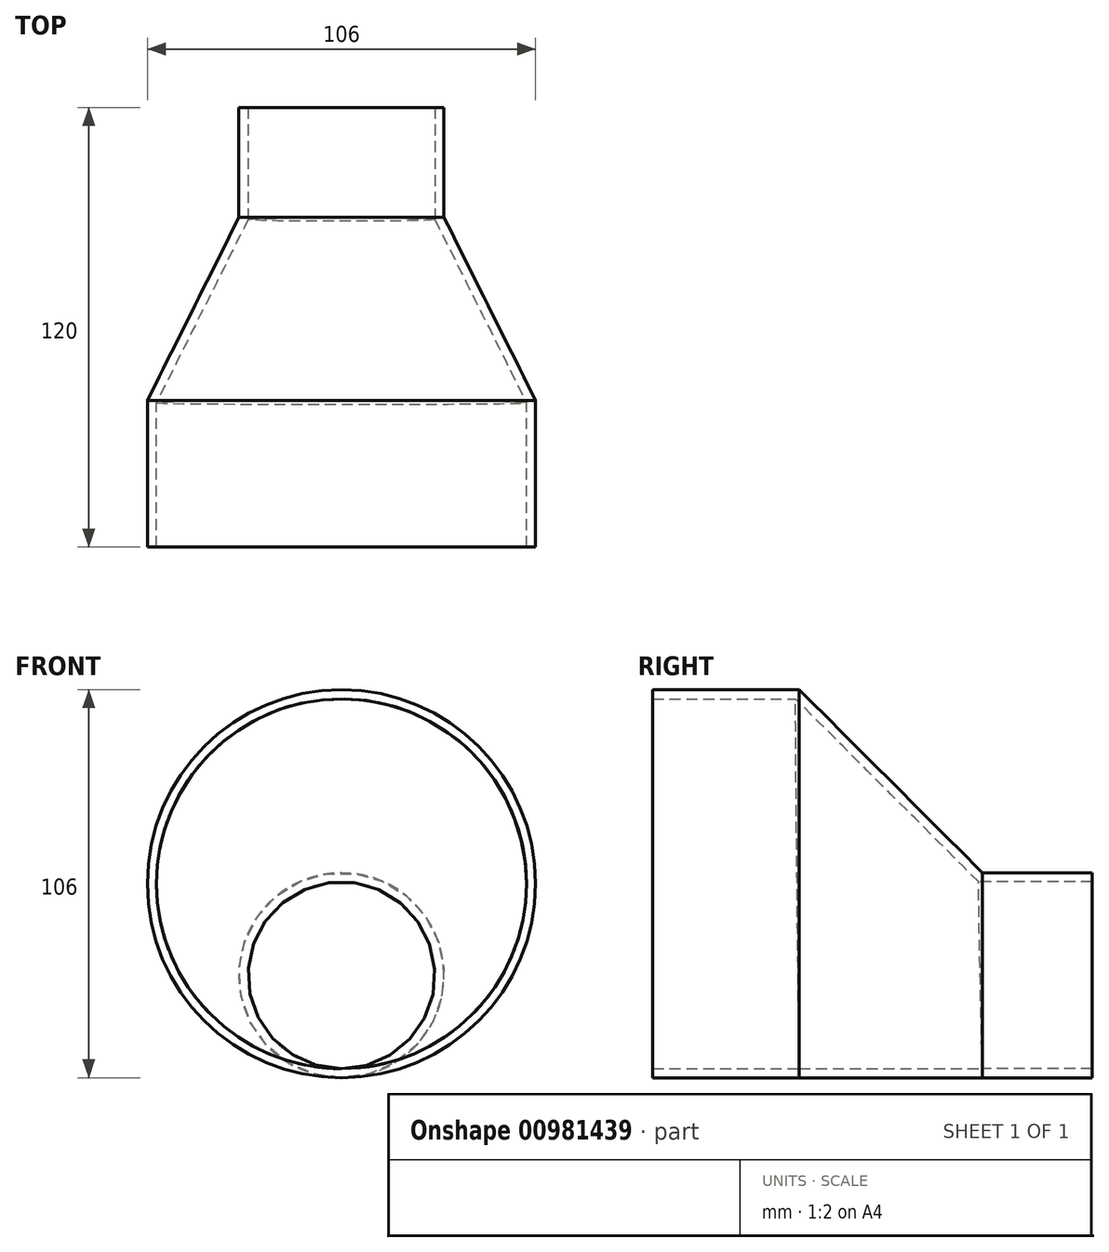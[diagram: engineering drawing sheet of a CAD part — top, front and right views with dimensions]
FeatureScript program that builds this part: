
annotation { "Feature Type Name" : "Feature", "Feature Type Description" : "" }
export const myFeature = defineFeature(function(context is Context, id is Id, definition is map)
    precondition{}
    {
        {
            var Q0;
            Q0=qCreatedBy(makeId("Front.planeOp"),FACE);
            var sketch = newSketch(context, id + "F0", { "sketchPlane" : qUnion([Q0])});
            skCircle(sketch, "E0", {"center": v(0, 0) * mm, "radius": 50 * mm});
            skCircle(sketch, "E1", {"center": v(0, 0) * mm, "radius": 53 * mm});
            skSolve(sketch);
        }
        {
            var Q0;
            Q0=makeQuery(id+"F0.imprint","IMPRINT",FACE,{"disambiguationData":[TD([[makeQuery(id+"F0.imprint","IMPRINT",EDGE,{"derivedFrom":sQuery(id+"F0.wireOp",EDGE,"E0")}),-1.0]])]});
            var Q1;
            Q1=makeQuery(id+"F0.imprint","IMPRINT",FACE,{"disambiguationData":[TD([[makeQuery(id+"F0.imprint","IMPRINT",EDGE,{"derivedFrom":sQuery(id+"F0.wireOp",EDGE,"E0")}),1.0]])]});
            extrude(context, id + "F1", {"entities" : qUnion([Q0, Q1]), "depth" : 40 * mm, "offsetDistance" : 25 * mm});
        }
        {
            var Q0;
            Q0=qCreatedBy(makeId("Front.planeOp"),FACE);
            cPlane(context, id + "F2", {"entities" : qUnion([Q0]), "cplaneType" : CPlaneType.OFFSET, "offset" : 50 * mm, "oppositeDirection" : true, "width" : 150 * mm, "height" : 150 * mm});
        }
        {
            var Q0;
            Q0=qCreatedBy(id+"F2.planeOp",FACE);
            var sketch = newSketch(context, id + "F3", { "sketchPlane" : qUnion([Q0])});
            skCircle(sketch, "E2", {"center": v(0, -25) * mm, "radius": 25 * mm});
            skCircle(sketch, "E3", {"center": v(0, -25) * mm, "radius": 28 * mm});
            skSolve(sketch);
        }
        {
            var Q0;
            Q0=makeQuery(id+"F3.imprint","IMPRINT",FACE,{"disambiguationData":[TD([[makeQuery(id+"F3.imprint","IMPRINT",EDGE,{"derivedFrom":sQuery(id+"F3.wireOp",EDGE,"E2")}),-1.0]])]});
            var Q1;
            Q1=makeQuery(id+"F3.imprint","IMPRINT",FACE,{"disambiguationData":[TD([[makeQuery(id+"F3.imprint","IMPRINT",EDGE,{"derivedFrom":sQuery(id+"F3.wireOp",EDGE,"E2")}),1.0]])]});
            extrude(context, id + "F4", {"entities" : qUnion([Q0, Q1]), "oppositeDirection" : true, "depth" : 30 * mm, "offsetDistance" : 25 * mm});
        }
        {
            var Q0;
            Q0=makeQuery(id+"F1.opExtrude","CAP_FACE",FACE,{"disambiguationData":[OSD([sQuery(id+"F0.wireOp",EDGE,"E1")])],"isStart":true});
            var Q1;
            Q1=makeQuery(id+"F4.opExtrude","CAP_FACE",FACE,{"disambiguationData":[OSD([sQuery(id+"F3.wireOp",EDGE,"E3")])],"isStart":true});
            loft(context, id + "F5", {"operationType" : NewBodyOperationType.ADD, "sheetProfilesArray" : [{ "sheetProfileEntities" : qUnion([Q0]) }, { "sheetProfileEntities" : qUnion([Q1]) }]});
        }
        {
            var Q0;
            Q0=makeQuery(id+"F1.opExtrude","CAP_FACE",FACE,{"disambiguationData":[OSD([sQuery(id+"F0.wireOp",EDGE,"E1")])],"isStart":false});
            var Q1;
            Q1=makeQuery(id+"F4.opExtrude","CAP_FACE",FACE,{"disambiguationData":[OSD([sQuery(id+"F3.wireOp",EDGE,"E3")])],"isStart":false});
            shell(context, id + "F6", {"entities" : qUnion([Q0, Q1]), "thickness" : 2.5 * mm});
        }
    });
